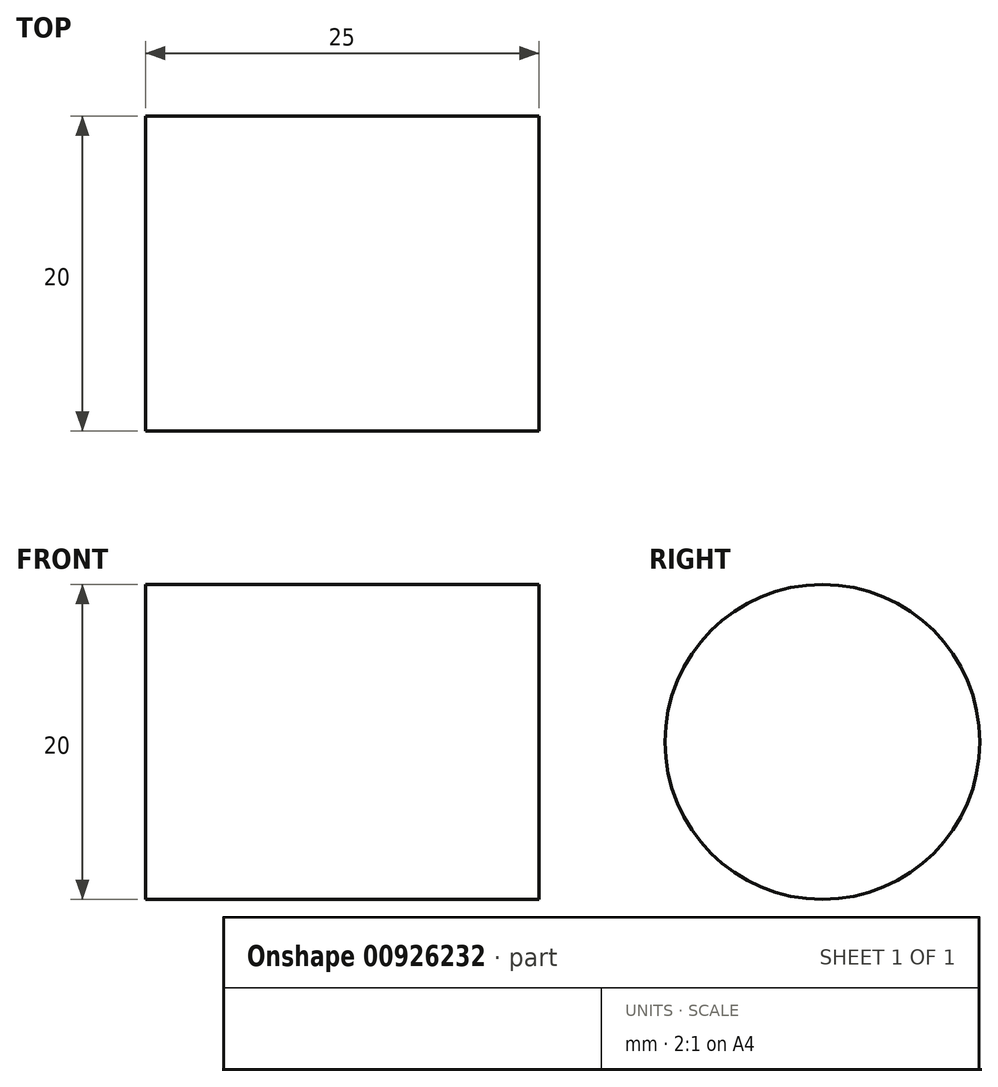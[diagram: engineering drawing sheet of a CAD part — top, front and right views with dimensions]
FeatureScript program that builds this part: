
annotation { "Feature Type Name" : "Feature", "Feature Type Description" : "" }
export const myFeature = defineFeature(function(context is Context, id is Id, definition is map)
    precondition{}
    {
        {
            var Q0;
            Q0=qCreatedBy(makeId("Right.planeOp"),FACE);
            var sketch = newSketch(context, id + "F0", { "sketchPlane" : qUnion([Q0])});
            skCircle(sketch, "E0", {"center": v(0, 0) * mm, "radius": 10 * mm});
            skSolve(sketch);
        }
        {
            var Q0;
            Q0 = qSketchRegion(id + "F0", true);
            var sketch = newSketch(context, id + "F1", { "sketchPlane" : qUnion([Q0])});
            skSolve(sketch);
        }
        {
            var Q0;
            Q0=makeQuery(id+"F1.imprint","IMPRINT",FACE,{"disambiguationData":[TD([[makeQuery(id+"F1.imprint","IMPRINT",EDGE,{"derivedFrom":makeQuery(id+"F0.imprint","IMPRINT",EDGE,{"derivedFrom":sQuery(id+"F0.wireOp",EDGE,"E0")})}),1.0]])]});
            extrude(context, id + "F2", {"entities" : qUnion([Q0]), "depth" : 25 * mm, "offsetDistance" : 25 * mm});
        }
    });
